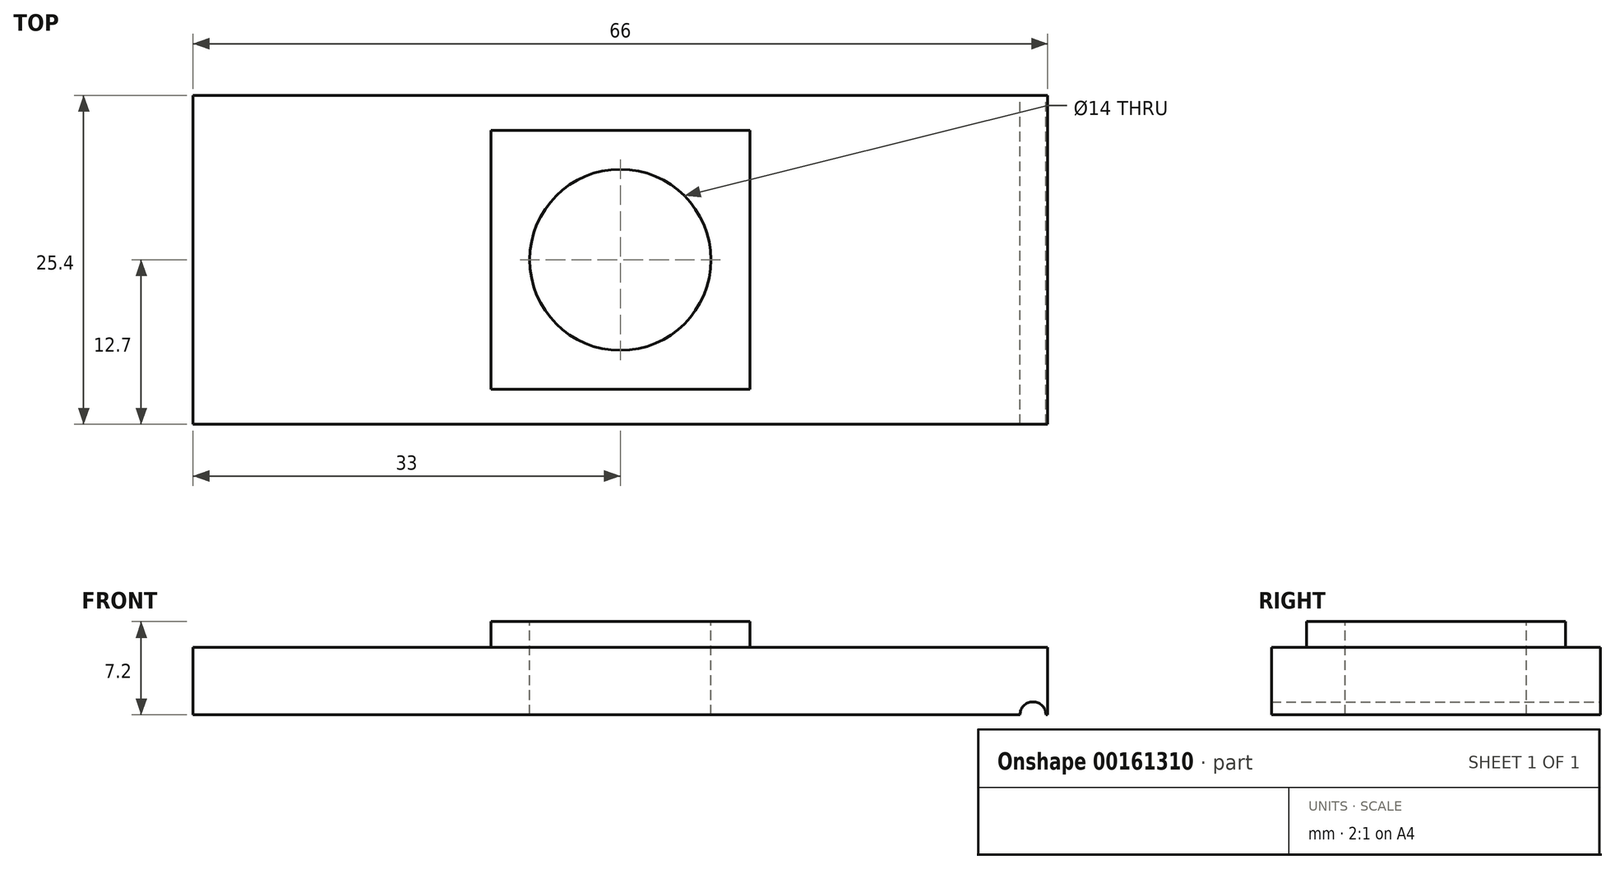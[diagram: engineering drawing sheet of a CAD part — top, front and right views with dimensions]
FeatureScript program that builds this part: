
annotation { "Feature Type Name" : "Feature", "Feature Type Description" : "" }
export const myFeature = defineFeature(function(context is Context, id is Id, definition is map)
    precondition{}
    {
        {
            var Q0;
            Q0=qCreatedBy(makeId("Top.planeOp"),FACE);
            var sketch = newSketch(context, id + "F0", { "sketchPlane" : qUnion([Q0])});
            skLineSegment(sketch, "E0.bottom", {"start": v(33, 12.7) * mm, "end": v(-33, 12.7) * mm});
            skLineSegment(sketch, "E0.top", {"start": v(33, -12.7) * mm, "end": v(-33, -12.7) * mm});
            skLineSegment(sketch, "E0.left", {"start": v(33, 12.7) * mm, "end": v(33, -12.7) * mm});
            skLineSegment(sketch, "E0.right", {"start": v(-33, 12.7) * mm, "end": v(-33, -12.7) * mm});
            skPoint(sketch, "E0.middle", {"position": v(0, 0) * mm});
            skSolve(sketch);
        }
        {
            var Q0;
            Q0=makeQuery(id+"F0.imprint","IMPRINT",FACE,{"disambiguationData":[TD([[makeQuery(id+"F0.imprint","IMPRINT",EDGE,{"derivedFrom":sQuery(id+"F0.wireOp",EDGE,"E0.bottom")}),1.0]])]});
            extrude(context, id + "F1", {"entities" : qUnion([Q0]), "depth" : 5.2 * mm});
        }
        {
            var Q0;
            Q0=makeQuery(id+"F1.opExtrude","CAP_FACE",FACE,{"disambiguationData":[OSD([sQuery(id+"F0.wireOp",EDGE,"E0.bottom"),sQuery(id+"F0.wireOp",EDGE,"E0.top"),sQuery(id+"F0.wireOp",EDGE,"E0.left"),sQuery(id+"F0.wireOp",EDGE,"E0.right")])],"isStart":false});
            var sketch = newSketch(context, id + "F2", { "sketchPlane" : qUnion([Q0])});
            skLineSegment(sketch, "E1.bottom", {"start": v(10, -10) * mm, "end": v(-10, -10) * mm});
            skLineSegment(sketch, "E1.top", {"start": v(10, 10) * mm, "end": v(-10, 10) * mm});
            skLineSegment(sketch, "E1.left", {"start": v(10, -10) * mm, "end": v(10, 10) * mm});
            skLineSegment(sketch, "E1.right", {"start": v(-10, -10) * mm, "end": v(-10, 10) * mm});
            skPoint(sketch, "E1.middle", {"position": v(0, 0) * mm});
            skSolve(sketch);
        }
        {
            var Q0;
            Q0 = qSketchRegion(id + "F2", true);
            extrude(context, id + "F3", {"entities" : qUnion([Q0]), "operationType" : NewBodyOperationType.ADD, "depth" : 2 * mm});
        }
        {
            var Q0;
            Q0=makeQuery(id+"F3.opExtrude","CAP_FACE",FACE,{"disambiguationData":[OSD([sQuery(id+"F2.wireOp",EDGE,"E1.bottom"),sQuery(id+"F2.wireOp",EDGE,"E1.top"),sQuery(id+"F2.wireOp",EDGE,"E1.left"),sQuery(id+"F2.wireOp",EDGE,"E1.right")])],"isStart":false});
            var sketch = newSketch(context, id + "F4", { "sketchPlane" : qUnion([Q0])});
            skCircle(sketch, "E2", {"center": v(0, 0) * mm, "radius": 7 * mm});
            skSolve(sketch);
        }
        {
            var Q0;
            Q0 = qSketchRegion(id + "F4", true);
            extrude(context, id + "F5", {"entities" : qUnion([Q0]), "operationType" : NewBodyOperationType.REMOVE, "oppositeDirection" : true, "depth" : 16.04 * mm});
        }
        {
            var Q0;
            Q0=qCreatedBy(makeId("Front.planeOp"),FACE);
            var sketch = newSketch(context, id + "F6", { "sketchPlane" : qUnion([Q0])});
            skCircle(sketch, "E3", {"center": v(31.87, 0) * mm, "radius": 1 * mm});
            skSolve(sketch);
        }
        {
            var Q0;
            Q0 = qSketchRegion(id + "F6", true);
            extrude(context, id + "F7", {"entities" : qUnion([Q0]), "operationType" : NewBodyOperationType.REMOVE, "depth" : 25 * mm, "hasSecondDirection" : true, "secondDirectionOppositeDirection" : true, "secondDirectionDepth" : 25 * mm});
        }
    });
